# Revit family: Showerhead-Rainshower-American_Standard-Universal-1660683_Series
name_source: partatom
category: Plumbing Fixtures
units: mm (PartAtom-declared; Revit-internal decimal feet)

## family parameters
Always vertical = No
Cut with Voids When Loaded = No
OmniClass Number = 23.45.05.14.17
OmniClass Title = Showers
Part Type = Normal
Room Calculation Point = No
Round Connector Dimension = Use Diameter
Shared = Yes
Work Plane-Based = Yes

## types (3) — shared parameters
Assembly Code = D2010710
CW Connection = No
CWFU = 3
Default Elevation = 0"
Description = 8" 2.5 gpm/9.5 L/min Round Fixed Showerhead
Diameter = 10"
Flow Rate = 2.5 gpm / 9.5 L/min.
HW Connection = No
HWFU = 3
IAPMO Compliance = ASME A112.18.1, IAPMO (cUPC)
Manufacturer = American Standard
Optional 1660.103- 3" Ceiling Mount Shower Arm = No
Optional 1660.118- 18" Wall Mount Right Angle Shower Arm = No
Optional 1660.186- 6" Ceiling Mount Shower Arm = No
Optional 1660.190- 12" Ceiling Mount Shower Arm = No
Optional 1660.191- Square Shower Arm Escutcheon = No
Optional 1660.194- 12" Wall Mount Right Angle Shower Arm = No
Price = Prices may vary. Please consult Manufacturer Representative for most up-to-date price list.
Product Documentation Link = https://americanstandard.box.com
Product Page URL = https://www.americanstandard-us.com
Revised Date = 05/25/2022
Tempered Water Connection = Yes
URL = https://www.americanstandard.ca
Vent Connection = No
WFU = 4
Waste Connection = No
Water Connection Diameter = 1/2"

## per-type parameters (varying)
| type | Finish | Material |
| 1660.683.002 | Brass-American Standard-002-Polished Chrome | Brass-American Standard-002-Polished Chrome |
| 1660.683.295 | Brass-American Standard-295-Brushed Nickel | Brass-American Standard-295-Brushed Nickel |
| 1660.683.243 | Brass-American Standard-243-Matte Black | Brass-American Standard-243-Matte Black |

note: column(s) folded — value = type name in every type: Model

## geometry (parser evidence)
native form markers: Sweep x3
no freeform markers — native parametric forms only
